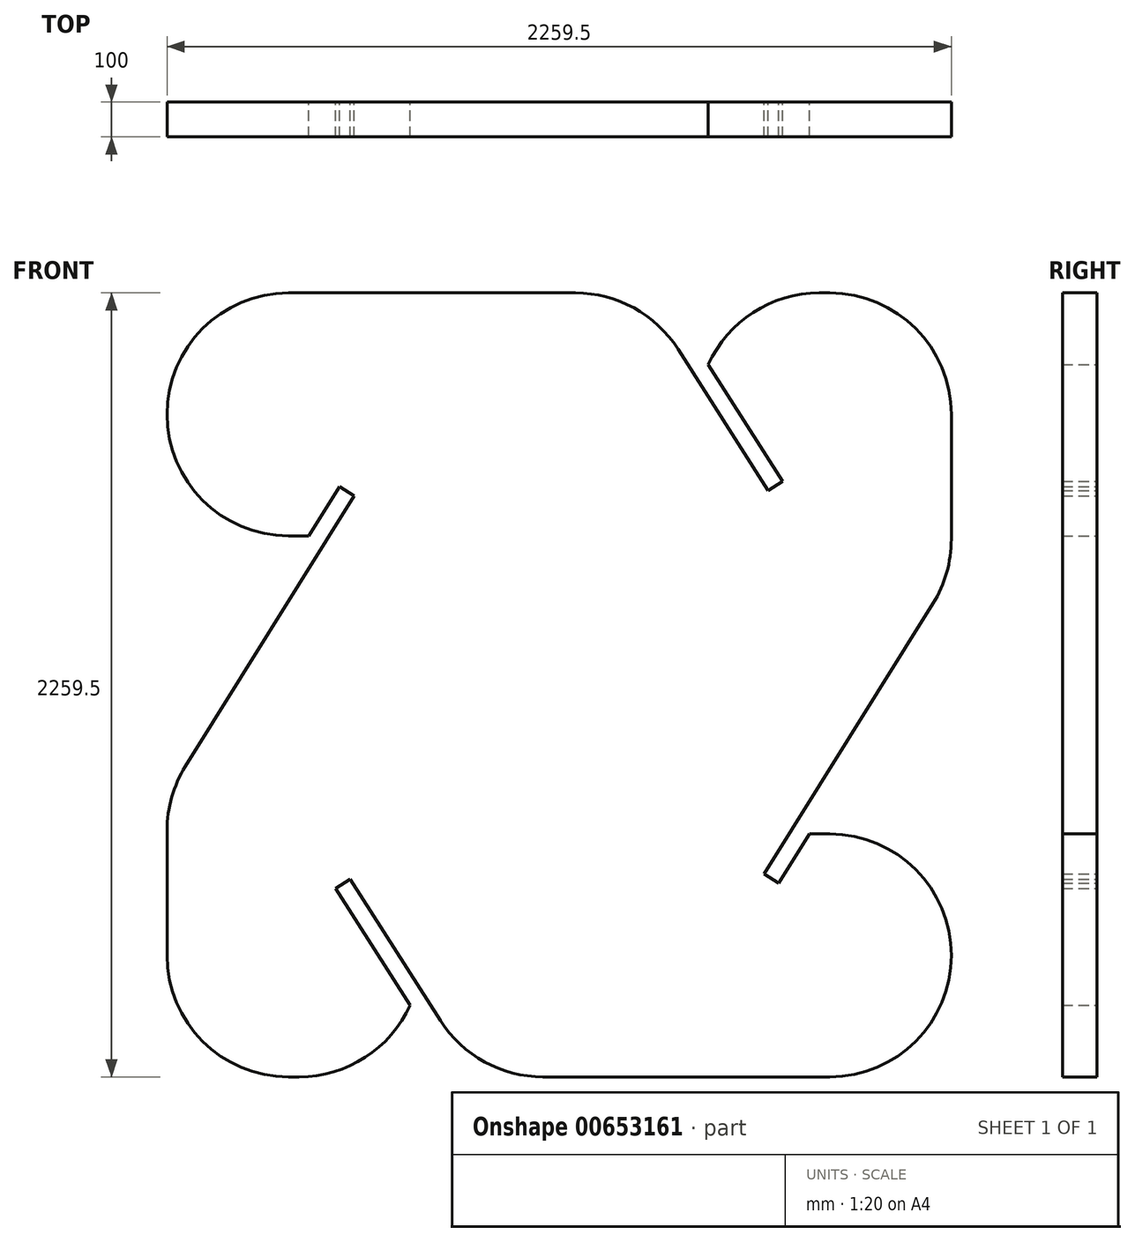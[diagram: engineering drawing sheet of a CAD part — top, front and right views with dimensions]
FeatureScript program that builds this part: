
annotation { "Feature Type Name" : "Feature", "Feature Type Description" : "" }
export const myFeature = defineFeature(function(context is Context, id is Id, definition is map)
    precondition{}
    {
        {
            var Q0;
            Q0=qCreatedBy(makeId("Front.planeOp"),FACE);
            var sketch = newSketch(context, id + "F0", { "sketchPlane" : qUnion([Q0])});
            skLineSegment(sketch, "E0", {"start": v(1129.75, 1129.75) * mm, "end": v(1129.75, 319.67) * mm});
            skLineSegment(sketch, "E1", {"start": v(-1129.75, -1129.75) * mm, "end": v(-1129.75, -319.67) * mm});
            skLineSegment(sketch, "E2", {"start": v(268.63, 1129.75) * mm, "end": v(622.98, 573.45) * mm, "construction": true});
            skLineSegment(sketch, "E3", {"start": v(1129.75, 272.44) * mm, "end": v(611.55, -558.2) * mm, "construction": true});
            skLineSegment(sketch, "E4", {"start": v(-268.63, -1129.75) * mm, "end": v(-622.98, -573.45) * mm, "construction": true});
            skLineSegment(sketch, "E5", {"start": v(-1129.75, -272.44) * mm, "end": v(-611.55, 558.2) * mm, "construction": true});
            skLineSegment(sketch, "E6", {"start": v(-721.16, 429.75) * mm, "end": v(-632.76, 571.44) * mm});
            skLineSegment(sketch, "E7", {"start": v(-632.76, 571.44) * mm, "end": v(-590.34, 544.98) * mm});
            skLineSegment(sketch, "E8", {"start": v(-590.34, 544.98) * mm, "end": v(-1129.75, -319.67) * mm});
            skLineSegment(sketch, "E9.trimOffspring", {"start": v(-1129.75, 429.75) * mm, "end": v(-1129.75, 1129.75) * mm});
            skLineSegment(sketch, "E10", {"start": v(-1129.75, 1129.75) * mm, "end": v(238.99, 1129.75) * mm});
            skLineSegment(sketch, "E11", {"start": v(1129.75, -1129.75) * mm, "end": v(-238.99, -1129.75) * mm});
            skLineSegment(sketch, "E12", {"start": v(-1129.75, 1129.75) * mm, "end": v(1129.75, -1129.75) * mm, "construction": true});
            skLineSegment(sketch, "E13", {"start": v(1129.75, 1129.75) * mm, "end": v(-1129.75, -1129.75) * mm, "construction": true});
            skLineSegment(sketch, "E14", {"start": v(-429.75, -923.33) * mm, "end": v(-644.07, -586.88) * mm});
            skLineSegment(sketch, "E15", {"start": v(-644.07, -586.88) * mm, "end": v(-601.9, -560.02) * mm});
            skLineSegment(sketch, "E16", {"start": v(-601.9, -560.02) * mm, "end": v(-238.99, -1129.75) * mm});
            skLineSegment(sketch, "E17", {"start": v(721.16, -429.75) * mm, "end": v(632.76, -571.44) * mm});
            skLineSegment(sketch, "E18", {"start": v(632.76, -571.44) * mm, "end": v(590.34, -544.98) * mm});
            skLineSegment(sketch, "E19", {"start": v(590.34, -544.98) * mm, "end": v(1129.75, 319.67) * mm});
            skLineSegment(sketch, "E20", {"start": v(429.75, 923.33) * mm, "end": v(644.07, 586.88) * mm});
            skLineSegment(sketch, "E21", {"start": v(644.07, 586.88) * mm, "end": v(601.9, 560.02) * mm});
            skLineSegment(sketch, "E22", {"start": v(601.9, 560.02) * mm, "end": v(238.99, 1129.75) * mm});
            skLineSegment(sketch, "E23", {"start": v(-1129.75, 429.75) * mm, "end": v(-721.16, 429.75) * mm});
            skLineSegment(sketch, "E24", {"start": v(-429.75, -1129.75) * mm, "end": v(-429.75, -923.33) * mm});
            skLineSegment(sketch, "E25", {"start": v(1129.75, -429.75) * mm, "end": v(721.16, -429.75) * mm});
            skLineSegment(sketch, "E26", {"start": v(429.75, 1129.75) * mm, "end": v(429.75, 923.33) * mm});
            skLineSegment(sketch, "E27.trimOffspring", {"start": v(429.75, 1129.75) * mm, "end": v(1129.75, 1129.75) * mm});
            skLineSegment(sketch, "E28.trimOffspring", {"start": v(-429.75, -1129.75) * mm, "end": v(-1129.75, -1129.75) * mm});
            skLineSegment(sketch, "E29.trimOffspring", {"start": v(1129.75, -429.75) * mm, "end": v(1129.75, -1129.75) * mm});
            skSolve(sketch);
        }
        {
            var Q0;
            Q0=makeQuery(id+"F0.imprint","IMPRINT",FACE,{"disambiguationData":[TD([[makeQuery(id+"F0.imprint","IMPRINT",EDGE,{"derivedFrom":sQuery(id+"F0.wireOp",EDGE,"E0")}),-1.0]])]});
            extrude(context, id + "F1", {"entities" : qUnion([Q0]), "depth" : 100 * mm, "offsetDistance" : 25 * mm});
        }
        {
            var Q0;
            Q0=makeQuery(id+"F1.opExtrude","SWEPT_EDGE",EDGE,{"disambiguationData":[OSD([sQuery(id+"F0.wireOp",EDGE,"E0"),sQuery(id+"F0.wireOp",EDGE,"E27.trimOffspring")])]});
            var Q1;
            Q1=makeQuery(id+"F1.opExtrude","SWEPT_EDGE",EDGE,{"disambiguationData":[OSD([sQuery(id+"F0.wireOp",EDGE,"E26"),sQuery(id+"F0.wireOp",EDGE,"E27.trimOffspring")])]});
            var Q2;
            Q2=makeQuery(id+"F1.opExtrude","SWEPT_EDGE",EDGE,{"disambiguationData":[OSD([sQuery(id+"F0.wireOp",EDGE,"E9.trimOffspring"),sQuery(id+"F0.wireOp",EDGE,"E10")])]});
            var Q3;
            Q3=makeQuery(id+"F1.opExtrude","SWEPT_EDGE",EDGE,{"disambiguationData":[OSD([sQuery(id+"F0.wireOp",EDGE,"E9.trimOffspring"),sQuery(id+"F0.wireOp",EDGE,"E23")])]});
            var Q4;
            Q4=makeQuery(id+"F1.opExtrude","SWEPT_EDGE",EDGE,{"disambiguationData":[OSD([sQuery(id+"F0.wireOp",EDGE,"E1"),sQuery(id+"F0.wireOp",EDGE,"E28.trimOffspring")])]});
            var Q5;
            Q5=makeQuery(id+"F1.opExtrude","SWEPT_EDGE",EDGE,{"disambiguationData":[OSD([sQuery(id+"F0.wireOp",EDGE,"E24"),sQuery(id+"F0.wireOp",EDGE,"E28.trimOffspring")])]});
            var Q6;
            Q6=makeQuery(id+"F1.opExtrude","SWEPT_EDGE",EDGE,{"disambiguationData":[OSD([sQuery(id+"F0.wireOp",EDGE,"E11"),sQuery(id+"F0.wireOp",EDGE,"E29.trimOffspring")])]});
            var Q7;
            Q7=makeQuery(id+"F1.opExtrude","SWEPT_EDGE",EDGE,{"disambiguationData":[OSD([sQuery(id+"F0.wireOp",EDGE,"E25"),sQuery(id+"F0.wireOp",EDGE,"E29.trimOffspring")])]});
            var Q8;
            Q8=makeQuery(id+"F1.opExtrude","SWEPT_EDGE",EDGE,{"disambiguationData":[OSD([sQuery(id+"F0.wireOp",EDGE,"E1"),sQuery(id+"F0.wireOp",EDGE,"E8")])]});
            var Q9;
            Q9=makeQuery(id+"F1.opExtrude","SWEPT_EDGE",EDGE,{"disambiguationData":[OSD([sQuery(id+"F0.wireOp",EDGE,"E11"),sQuery(id+"F0.wireOp",EDGE,"E16")])]});
            var Q10;
            Q10=makeQuery(id+"F1.opExtrude","SWEPT_EDGE",EDGE,{"disambiguationData":[OSD([sQuery(id+"F0.wireOp",EDGE,"E0"),sQuery(id+"F0.wireOp",EDGE,"E19")])]});
            var Q11;
            Q11=makeQuery(id+"F1.opExtrude","SWEPT_EDGE",EDGE,{"disambiguationData":[OSD([sQuery(id+"F0.wireOp",EDGE,"E10"),sQuery(id+"F0.wireOp",EDGE,"E22")])]});
            fillet(context, id + "F2", {"entities" : qUnion([Q0, Q1, Q2, Q3, Q4, Q5, Q6, Q7, Q8, Q9, Q10, Q11]), "radius" : 350 * mm, "tangentPropagation" : true, "allowEdgeOverflow" : false});
        }
    });
